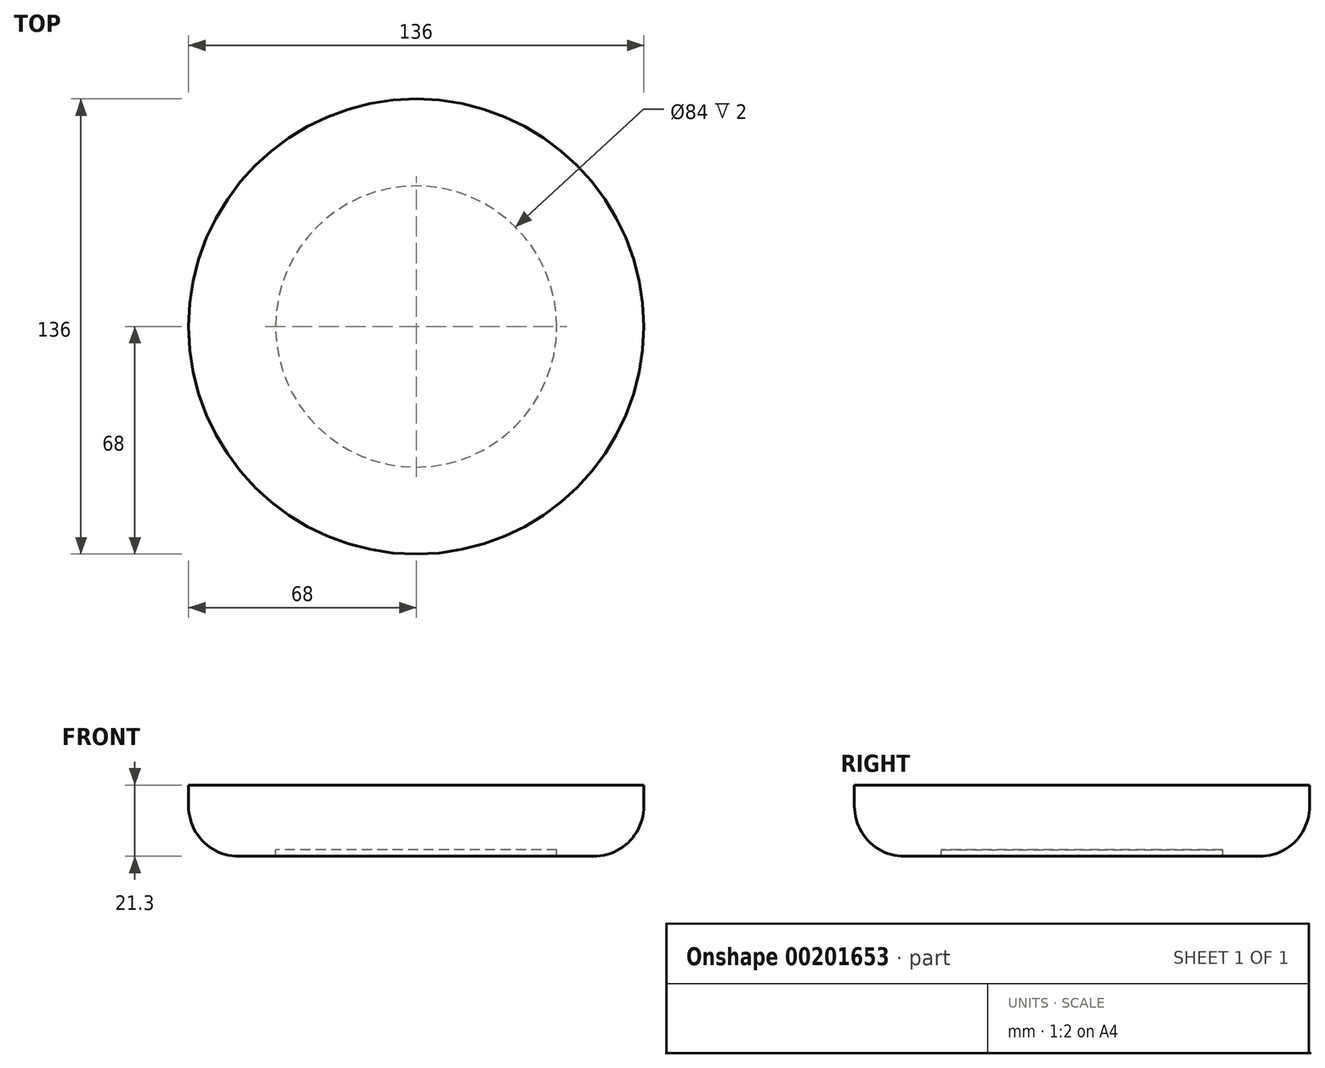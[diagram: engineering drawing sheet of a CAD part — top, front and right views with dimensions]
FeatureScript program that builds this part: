
annotation { "Feature Type Name" : "Feature", "Feature Type Description" : "" }
export const myFeature = defineFeature(function(context is Context, id is Id, definition is map)
    precondition{}
    {
        {
            var Q0;
            Q0=qCreatedBy(makeId("Front.planeOp"),FACE);
            var sketch = newSketch(context, id + "F0", { "sketchPlane" : qUnion([Q0])});
            skLineSegment(sketch, "E0.bottom", {"start": v(0, 0) * mm, "end": v(-68, 0) * mm});
            skLineSegment(sketch, "E0.top", {"start": v(-42, -21.3) * mm, "end": v(-53, -21.3) * mm});
            skLineSegment(sketch, "E0.left", {"start": v(0, 0) * mm, "end": v(0, -19.3) * mm});
            skLineSegment(sketch, "E0.right", {"start": v(-68, 0) * mm, "end": v(-68, -6.3) * mm});
            skLineSegment(sketch, "E1.top", {"start": v(0, -19.3) * mm, "end": v(-42, -19.3) * mm});
            skLineSegment(sketch, "E1.right", {"start": v(-42, -21.3) * mm, "end": v(-42, -19.3) * mm});
            skPoint(sketch, "E2.visualSharp", {"position": v(-68, -21.3) * mm});
            skArc(sketch, "E2.filletArc", {"start": v(-68, -6.3) * mm, "mid": v(-63.6, -16.9) * mm, "end": v(-53, -21.3) * mm});
            skSolve(sketch);
        }
        {
            var Q0;
            Q0=makeQuery(id+"F0.imprint","IMPRINT",FACE,{"disambiguationData":[TD([[makeQuery(id+"F0.imprint","IMPRINT",EDGE,{"derivedFrom":sQuery(id+"F0.wireOp",EDGE,"E0.bottom")}),1.0]])]});
            var Q1;
            Q1=sQuery(id+"F0.wireOp",EDGE,"E0.left");
            revolve(context, id + "F1", {"entities" : qUnion([Q0]), "axis" : qUnion([Q1]), "revolveType" : RevolveType.FULL});
        }
    });
